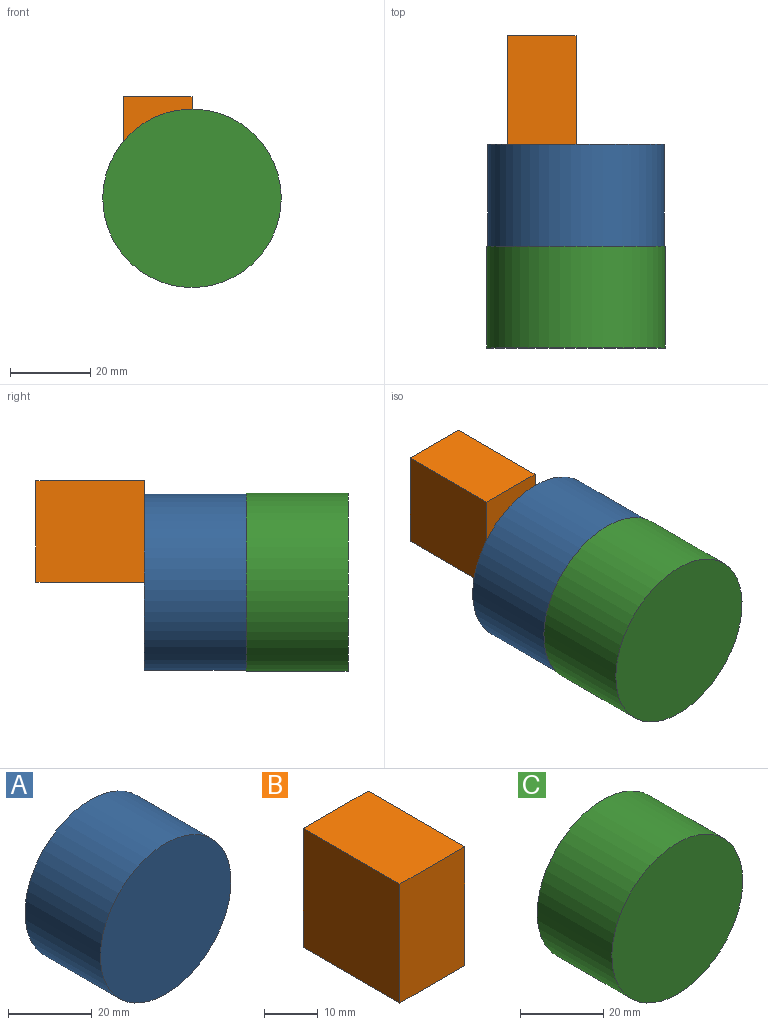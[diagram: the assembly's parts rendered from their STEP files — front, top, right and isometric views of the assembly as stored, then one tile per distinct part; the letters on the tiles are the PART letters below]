
ASSEMBLY  parts=3 mates=2
PART A: 3 faces, bbox 44x25.4x44 mm
  f0: cylinder r=21.99mm len=43.99mm, axis (0,1,0), area 3509.8mm2, adj f1,f2
  f1: plane 43.99x43.99mm, normal (0,-1,0), area 1519.5mm2, adj f0
  f2: plane 43.99x43.99mm, normal (0,1,0), area 1519.5mm2, adj f0
PART B: 6 faces, bbox 17x25.4x27.1 mm
  f0: plane 25.4x17.05mm, normal (0,0,1), area 433mm2, adj f1,f3,f4,f5
  f1: plane 27.08x25.4mm, normal (-1,0,0), area 687.9mm2, adj f0,f2,f4,f5
  f2: plane 25.4x17.05mm, normal (0,0,-1), area 433mm2, adj f1,f3,f4,f5
  f3: plane 27.08x25.4mm, normal (1,0,0), area 687.9mm2, adj f0,f2,f4,f5
  f4: plane 27.08x17.05mm, normal (0,-1,0), area 461.7mm2, adj f0,f1,f2,f3
  f5: plane 27.08x17.05mm, normal (0,1,0), area 461.7mm2, adj f0,f1,f2,f3
PART C: 3 faces, bbox 44.5x25.4x44.5 mm
  f0: cylinder r=22.27mm len=44.54mm, axis (0,1,0), area 3554.1mm2, adj f1,f2
  f1: plane 44.54x44.54mm, normal (0,-1,0), area 1558.1mm2, adj f0
  f2: plane 44.54x44.54mm, normal (0,1,0), area 1558.1mm2, adj f0
PLACE A t=(-32.7,-12.49,23.06)mm
PLACE B rot(axis=(1,0,0),90deg) t=(-6.38,61.18,5.45)mm
PLACE C t=(-125.12,-37.89,-94.54)mm
MATE revolute C.f0 <-> A.f0  axis (0,1,0) through (-43.91,-37.89,-19.95)mm
MATE fastened B.f0 <-> A.f0  axis (0,-1,0) through (-43.91,-12.49,-19.95)mm
